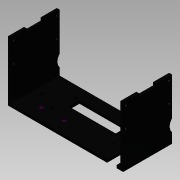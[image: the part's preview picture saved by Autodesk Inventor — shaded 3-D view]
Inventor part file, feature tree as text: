
AUTODESK INVENTOR PART (.ipt)
format: ipt  version: 2015 SP1 (Build 190203100, 203)  size: 232,960 bytes
history: native  units: mm
features: reference x18, extrude x10, sketch x9, plane x1
ambient origin geometry x8: Origin, YZ Plane, XZ Plane, XY Plane, X Axis, Y Axis, Z Axis, Center Point
bodies: Solid1 (feature_tree)
feature tree (38):
  sketch  "Sketch1"  dims[d0=120.812mm d1=51.214111mm]
  extrude  "Extrusion1"  Depth=51.214111mm
  extrude  "Extrusion2"  Depth=63.0mm TaperAngle=0.0deg
  plane  "Work Plane2"
  extrude  "Extrusion3"  Depth=3.0mm
  extrude  "Extrusion4"  [1 undecoded]
  extrude  "Extrusion5"  Depth=3.5mm
  extrude  "Extrusion7"  Depth=3.5mm
  extrude  "Extrusion8"  Depth=17.5mm
  extrude  "Extrusion9"  Depth=10.0mm TaperAngle=0.0deg
  extrude  "Extrusion11"  Depth=10.0mm TaperAngle=0.0deg
  extrude  "Extrusion12"  Depth=10.0mm
  sketch  "Sketch2"  dims[d4=3.0mm d5=0.0mm d6=63.0mm d7=0.0mm]
  reference  "Reference1"
  reference  "Reference2"
  reference  "Reference3"
  reference  "Reference4"
  sketch  "Sketch4"  dims[d8=3.0mm d9=3.0mm]
  sketch  "Sketch6"  dims[d10=114.812mm d11=-18.417445mm]
  reference  "Reference5"
  reference  "Reference6"
  sketch  "Sketch9"  dims[d12=3.5mm d13=3.5mm]
  reference  "Reference8"
  reference  "Reference9"
  reference  "Reference10"
  reference  "Reference11"
  sketch  "Sketch10"  dims[d14=3.5mm d15=3.5mm]
  sketch  "Sketch11"  dims[d16=10.0mm d17=0.0mm d18=17.5mm]
  reference  "Reference13"
  reference  "Reference14"
  reference  "Reference15"
  sketch  "Sketch15"  dims[d19=3.0mm d20=0.0mm d21=10.0mm d22=0.0mm]
  reference  "Reference21"
  sketch  "Sketch16"  dims[d25=200.0mm d26=0.0mm d29=10.0mm d30=0.0mm d31=3.5mm d32=3.5mm d33=2.0mm d34=2.0mm d35=10.0mm d36=0.0mm d37=2.0mm d38=2.0mm d39=90.0deg d47=10.0mm d48=0.0mm d49=10.0mm d50=17.5mm d51=10.0mm d52=0.0mm]
  reference  "Reference22"
  reference  "Reference23"
  reference  "Reference24"
  reference  "Reference25"
note: 1 required parameter value undecoded (feature->parameter linkage not recoverable at this tier; creation-order binding heuristic only, values carry confidence <= 0.55)
